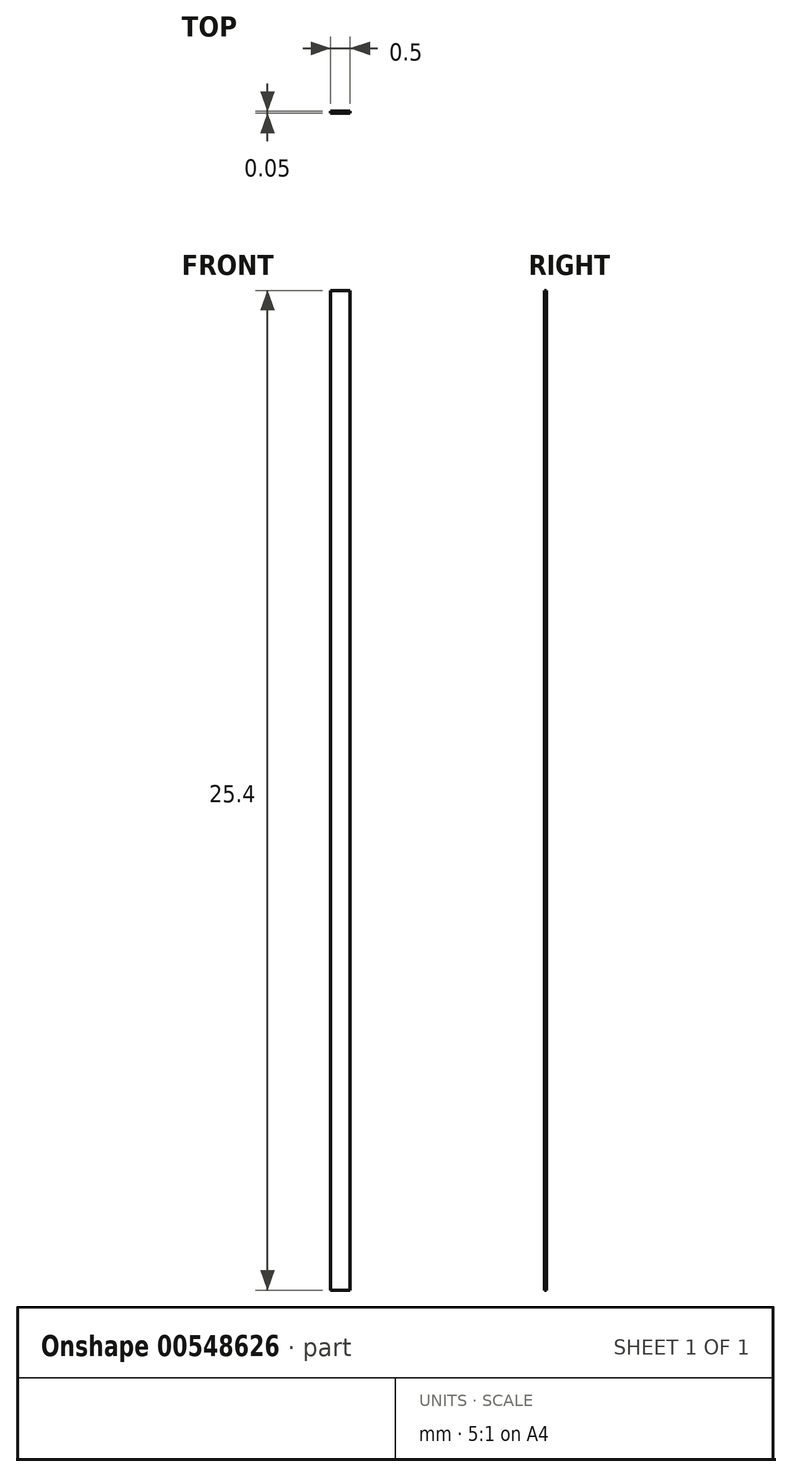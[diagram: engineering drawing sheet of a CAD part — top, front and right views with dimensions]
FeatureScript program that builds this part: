
annotation { "Feature Type Name" : "Feature", "Feature Type Description" : "" }
export const myFeature = defineFeature(function(context is Context, id is Id, definition is map)
    precondition{}
    {
        {
            var Q0;
            Q0=qCreatedBy(makeId("Front.planeOp"),FACE);
            var sketch = newSketch(context, id + "F0", { "sketchPlane" : qUnion([Q0])});
            skLineSegment(sketch, "E0.bottom", {"start": v(-0.5, 13.48) * mm, "end": v(0, 13.48) * mm});
            skLineSegment(sketch, "E0.top", {"start": v(-0.5, -11.92) * mm, "end": v(0, -11.92) * mm});
            skLineSegment(sketch, "E0.left", {"start": v(-0.5, 13.48) * mm, "end": v(-0.5, -11.92) * mm});
            skLineSegment(sketch, "E0.right", {"start": v(0, 13.48) * mm, "end": v(0, -11.92) * mm});
            skSolve(sketch);
        }
        {
            var Q0;
            Q0 = qSketchRegion(id + "F0", true);
            extrude(context, id + "F1", {"entities" : qUnion([Q0]), "depth" : 0.05 * mm, "offsetDistance" : 25.4 * mm});
        }
    });
